# Revit family: 3WayPod_08
name_source: partatom
category: Furniture
revit_build: Autodesk Revit 2013 (Build: 20120221_2030(x64)
units: mm (PartAtom-declared; Revit-internal decimal feet)

## types (8) — shared parameters
Glides, Top cap, Inner = <By Category>
Screen Fabric = <By Category>
Screen Frame = <By Category>
Workstation Frame = <By Category>
Worktop = <By Category>
Worktop Depth 1A = 750 mm  [stored 2.46063 ft]
Worktop Depth 1B = 750 mm  [stored 2.46063 ft]
Worktop Depth 2A = 750 mm  [stored 2.46063 ft]
Worktop Depth 2B = 750 mm  [stored 2.46063 ft]
Worktop Depth 3A = 750 mm  [stored 2.46063 ft]
Worktop Depth 3B = 750 mm  [stored 2.46063 ft]

## per-type parameters (varying)
| type | Auto Half Screen Thickness | Auto Half Screen Thickness 2 | Auto Half Screen Thickness 3 | Half Actual Screen Frame Thickness | Half Acutal Screen Frame Thickness | Half Panel Thickness Neg | Half Panel thickness | Screen Height AFL | Screen Length | Screen Thickness | Screen Thickness 2 | Screen thickness 3 | Worktop Length 1A | Worktop Length 2A | Worktop Length 3A |
| 1200Lx1200Lx750D, Z50@1200AFL | 25 mm  [stored 0.082021 ft] | 25 mm  [stored 0.082021 ft] | 25 mm  [stored 0.082021 ft] | 25 mm  [stored 0.082021 ft] | -25 mm  [stored -0.082021 ft] | -22 mm  [stored -0.0721785 ft] | 22 mm  [stored 0.0721785 ft] | 1200 mm | 1187 mm | 50 mm  [stored 0.164042 ft] | 50 mm  [stored 0.164042 ft] | 50 mm  [stored 0.164042 ft] | 1200 mm | 1200 mm | 1200 mm |
| 1200Lx1200Lx750D, Z22@1200AFL | 11 mm  [stored 0.0360892 ft] | 11 mm  [stored 0.0360892 ft] | 11 mm  [stored 0.0360892 ft] | 11 mm  [stored 0.0360892 ft] | -11 mm  [stored -0.0360892 ft] | -8 mm | 8 mm  [stored 0.0262467 ft] | 1200 mm | 1187 mm | 22 mm  [stored 0.0721785 ft] | 22 mm  [stored 0.0721785 ft] | 22 mm  [stored 0.0721785 ft] | 1200 mm | 1200 mm | 1200 mm |
| 1200Lx1200Lx750D, Z22@1350AFL | 11 mm  [stored 0.0360892 ft] | 11 mm  [stored 0.0360892 ft] | 11 mm  [stored 0.0360892 ft] | 11 mm  [stored 0.0360892 ft] | -11 mm  [stored -0.0360892 ft] | -8 mm | 8 mm  [stored 0.0262467 ft] | 1350 mm  [stored 4.42913 ft] | 1187 mm | 22 mm  [stored 0.0721785 ft] | 22 mm  [stored 0.0721785 ft] | 22 mm  [stored 0.0721785 ft] | 1200 mm | 1200 mm | 1200 mm |
| 1200Lx1200Lx750D, Z50@1350AFL | 25 mm  [stored 0.082021 ft] | 25 mm  [stored 0.082021 ft] | 25 mm  [stored 0.082021 ft] | 25 mm  [stored 0.082021 ft] | -25 mm  [stored -0.082021 ft] | -22 mm  [stored -0.0721785 ft] | 22 mm  [stored 0.0721785 ft] | 1350 mm  [stored 4.42913 ft] | 1187 mm | 50 mm  [stored 0.164042 ft] | 50 mm  [stored 0.164042 ft] | 50 mm  [stored 0.164042 ft] | 1200 mm | 1200 mm | 1200 mm |
| 1350Lx1350Lx750D, Z22@1200AFL | 11 mm  [stored 0.0360892 ft] | 11 mm  [stored 0.0360892 ft] | 11 mm  [stored 0.0360892 ft] | 11 mm  [stored 0.0360892 ft] | -11 mm  [stored -0.0360892 ft] | -8 mm | 8 mm  [stored 0.0262467 ft] | 1200 mm | 1337 mm | 22 mm  [stored 0.0721785 ft] | 22 mm  [stored 0.0721785 ft] | 22 mm  [stored 0.0721785 ft] | 1350 mm  [stored 4.42913 ft] | 1350 mm  [stored 4.42913 ft] | 1350 mm  [stored 4.42913 ft] |
| 1350Lx1350Lx750D, Z22@1350AFL | 11 mm  [stored 0.0360892 ft] | 11 mm  [stored 0.0360892 ft] | 11 mm  [stored 0.0360892 ft] | 11 mm  [stored 0.0360892 ft] | -11 mm  [stored -0.0360892 ft] | -8 mm | 8 mm  [stored 0.0262467 ft] | 1350 mm  [stored 4.42913 ft] | 1337 mm | 22 mm  [stored 0.0721785 ft] | 22 mm  [stored 0.0721785 ft] | 22 mm  [stored 0.0721785 ft] | 1350 mm  [stored 4.42913 ft] | 1350 mm  [stored 4.42913 ft] | 1350 mm  [stored 4.42913 ft] |
| 1350Lx1350Lx750D, Z50@1350AFL | 25 mm  [stored 0.082021 ft] | 25 mm  [stored 0.082021 ft] | 25 mm  [stored 0.082021 ft] | 25 mm  [stored 0.082021 ft] | -25 mm  [stored -0.082021 ft] | -22 mm  [stored -0.0721785 ft] | 22 mm  [stored 0.0721785 ft] | 1350 mm  [stored 4.42913 ft] | 1337 mm | 50 mm  [stored 0.164042 ft] | 50 mm  [stored 0.164042 ft] | 50 mm  [stored 0.164042 ft] | 1350 mm  [stored 4.42913 ft] | 1350 mm  [stored 4.42913 ft] | 1350 mm  [stored 4.42913 ft] |
| 1350Lx1350Lx750D, Z50@1200AFL | 25 mm  [stored 0.082021 ft] | 25 mm  [stored 0.082021 ft] | 25 mm  [stored 0.082021 ft] | 25 mm  [stored 0.082021 ft] | -25 mm  [stored -0.082021 ft] | -22 mm  [stored -0.0721785 ft] | 22 mm  [stored 0.0721785 ft] | 1200 mm | 1337 mm | 50 mm  [stored 0.164042 ft] | 50 mm  [stored 0.164042 ft] | 50 mm  [stored 0.164042 ft] | 1350 mm  [stored 4.42913 ft] | 1350 mm  [stored 4.42913 ft] | 1350 mm  [stored 4.42913 ft] |

note: [stored X ft] marks values corroborated as IEEE doubles in the binary element streams (Revit-internal decimal feet)

## geometry (parser evidence)
native form markers: Sweep x2
no freeform markers — native parametric forms only
